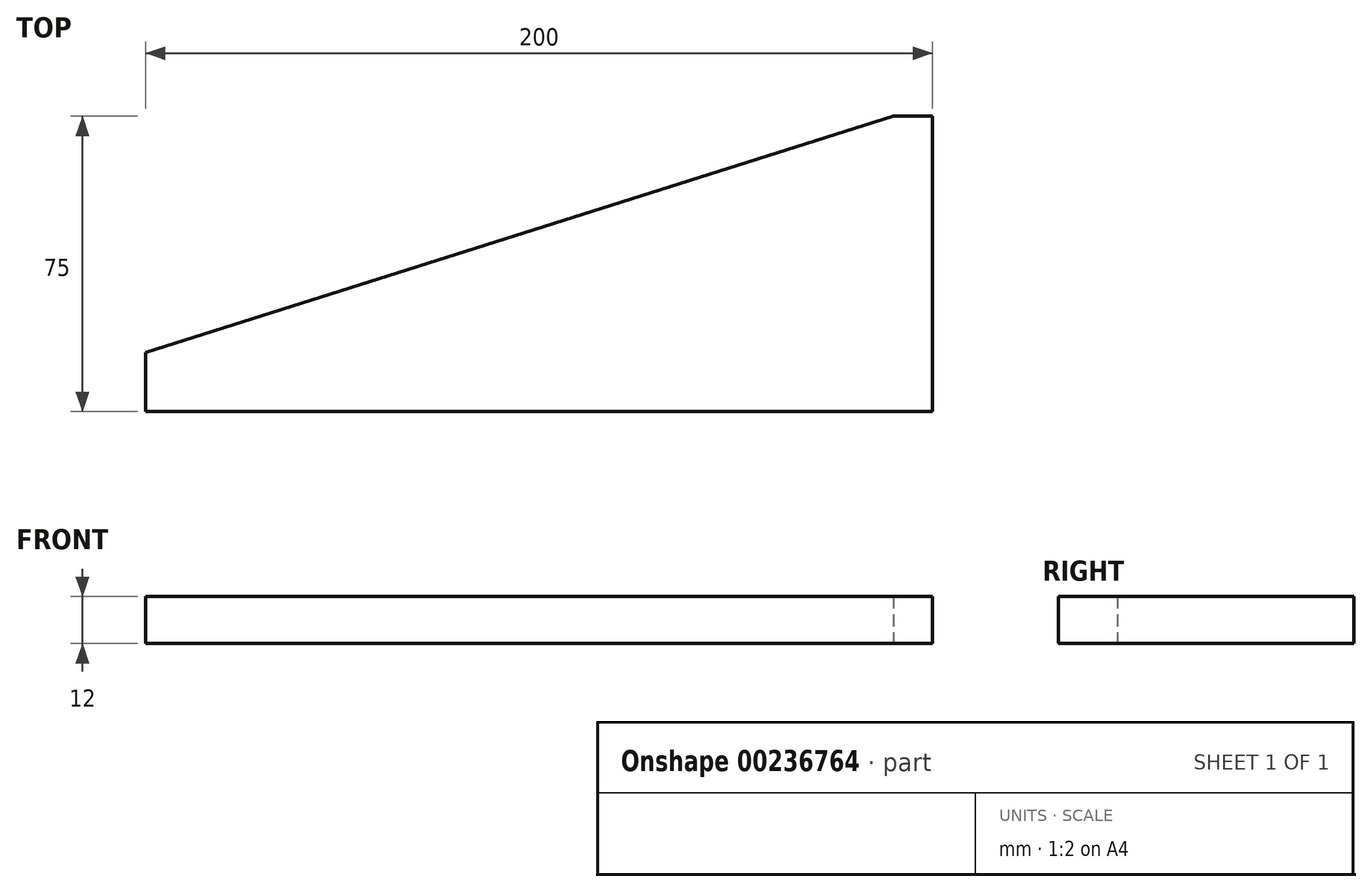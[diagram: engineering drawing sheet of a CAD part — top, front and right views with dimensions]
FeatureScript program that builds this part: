
annotation { "Feature Type Name" : "Feature", "Feature Type Description" : "" }
export const myFeature = defineFeature(function(context is Context, id is Id, definition is map)
    precondition{}
    {
        {
            var Q0;
            Q0=qCreatedBy(makeId("Top.planeOp"),FACE);
            var sketch = newSketch(context, id + "F0", { "sketchPlane" : qUnion([Q0])});
            skLineSegment(sketch, "E0.bottom", {"start": v(100, 37.5) * mm, "end": v(90, 37.5) * mm});
            skLineSegment(sketch, "E0.top", {"start": v(100, -37.5) * mm, "end": v(-100, -37.5) * mm});
            skLineSegment(sketch, "E0.left", {"start": v(100, 37.5) * mm, "end": v(100, -37.5) * mm});
            skLineSegment(sketch, "E0.right", {"start": v(-100, -22.5) * mm, "end": v(-100, -37.5) * mm});
            skPoint(sketch, "E0.middle", {"position": v(0, 0) * mm});
            skLineSegment(sketch, "E1", {"start": v(-100, -22.5) * mm, "end": v(90, 37.5) * mm});
            skPoint(sketch, "E2.orphan", {"position": v(-100, 37.5) * mm});
            skSolve(sketch);
        }
        {
            var Q0;
            Q0 = qSketchRegion(id + "F0", true);
            extrude(context, id + "F1", {"entities" : qUnion([Q0]), "depth" : 12 * mm, "offsetDistance" : 25 * mm});
        }
    });
